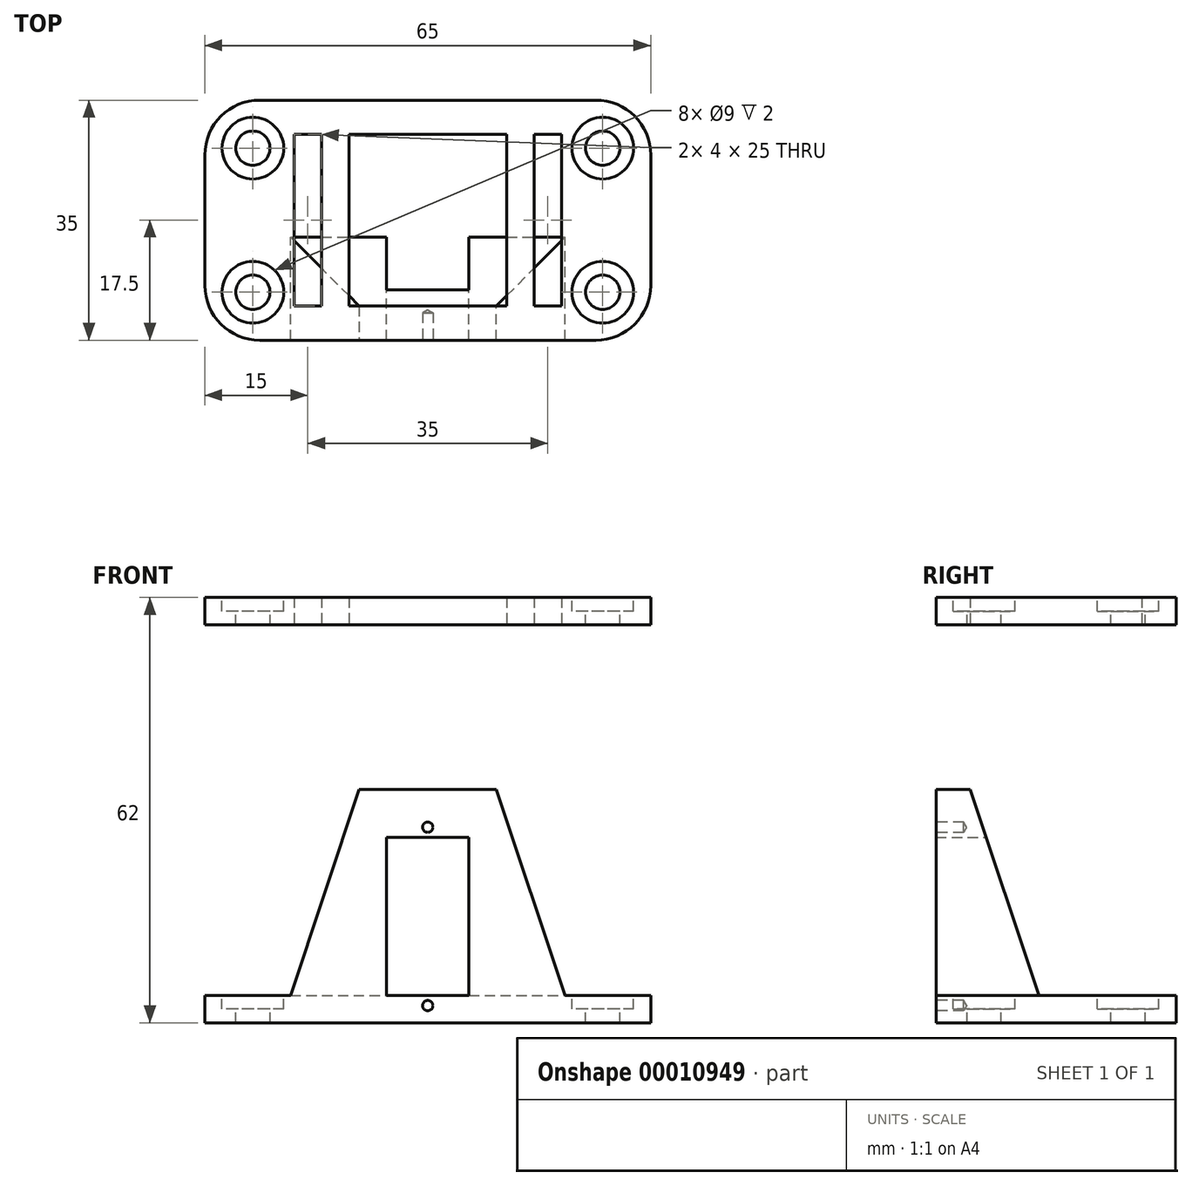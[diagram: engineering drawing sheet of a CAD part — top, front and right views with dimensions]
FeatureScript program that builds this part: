
annotation { "Feature Type Name" : "Feature", "Feature Type Description" : "" }
export const myFeature = defineFeature(function(context is Context, id is Id, definition is map)
    precondition{}
    {
        {
            var Q0;
            Q0=qCreatedBy(makeId("Top.planeOp"),FACE);
            var sketch = newSketch(context, id + "F0", { "sketchPlane" : qUnion([Q0])});
            skLineSegment(sketch, "E0.rect.bottom", {"start": v(-32.5, -17.5) * mm, "end": v(32.5, -17.5) * mm});
            skLineSegment(sketch, "E0.rect.top", {"start": v(-32.5, 17.5) * mm, "end": v(32.5, 17.5) * mm});
            skLineSegment(sketch, "E0.rect.left", {"start": v(-32.5, -17.5) * mm, "end": v(-32.5, 17.5) * mm});
            skLineSegment(sketch, "E0.rect.right", {"start": v(32.5, -17.5) * mm, "end": v(32.5, 17.5) * mm});
            skPoint(sketch, "E0.rect.middle", {"position": v(0, 0) * mm});
            skLineSegment(sketch, "E1", {"start": v(0, 0) * mm, "end": v(17.5, 0) * mm, "construction": true});
            skLineSegment(sketch, "E2.rect.bottom", {"start": v(19.5, -12.5) * mm, "end": v(15.5, -12.5) * mm});
            skLineSegment(sketch, "E2.rect.top", {"start": v(19.5, 12.5) * mm, "end": v(15.5, 12.5) * mm});
            skLineSegment(sketch, "E2.rect.left", {"start": v(19.5, -12.5) * mm, "end": v(19.5, 12.5) * mm});
            skLineSegment(sketch, "E2.rect.right", {"start": v(15.5, -12.5) * mm, "end": v(15.5, 12.5) * mm});
            skPoint(sketch, "E2.rect.middle", {"position": v(17.5, 0) * mm});
            skLineSegment(sketch, "E3", {"start": v(0, 0) * mm, "end": v(0, -46.23) * mm, "construction": true});
            skLineSegment(sketch, "E4.0.MirrorCS", {"start": v(-19.5, -12.5) * mm, "end": v(-15.5, -12.5) * mm});
            skLineSegment(sketch, "E5.0.MirrorCS", {"start": v(-19.5, -12.5) * mm, "end": v(-19.5, 12.5) * mm});
            skLineSegment(sketch, "E6.0.MirrorCS", {"start": v(-15.5, -12.5) * mm, "end": v(-15.5, 12.5) * mm});
            skLineSegment(sketch, "E7.0.MirrorCS", {"start": v(-19.5, 12.5) * mm, "end": v(-15.5, 12.5) * mm});
            skLineSegment(sketch, "E8.rect.bottom", {"start": v(11.5, -12.5) * mm, "end": v(-11.5, -12.5) * mm});
            skLineSegment(sketch, "E8.rect.top", {"start": v(11.5, 12.5) * mm, "end": v(-11.5, 12.5) * mm});
            skLineSegment(sketch, "E8.rect.left", {"start": v(11.5, -12.5) * mm, "end": v(11.5, 12.5) * mm});
            skLineSegment(sketch, "E8.rect.right", {"start": v(-11.5, -12.5) * mm, "end": v(-11.5, 12.5) * mm});
            skSolve(sketch);
        }
        {
            var Q0;
            Q0=makeQuery(id+"F0.imprint","IMPRINT",FACE,{"disambiguationData":[TD([[makeQuery(id+"F0.imprint","IMPRINT",EDGE,{"derivedFrom":sQuery(id+"F0.wireOp",EDGE,"E0.rect.bottom")}),1.0]])]});
            extrude(context, id + "F1", {"entities" : qUnion([Q0]), "depth" : 4 * mm});
        }
        {
            var Q0;
            Q0=makeQuery(id+"F1.opExtrude","CAP_FACE",FACE,{"disambiguationData":[OSD([sQuery(id+"F0.wireOp",EDGE,"E0.rect.bottom"),sQuery(id+"F0.wireOp",EDGE,"E0.rect.top"),sQuery(id+"F0.wireOp",EDGE,"E0.rect.left"),sQuery(id+"F0.wireOp",EDGE,"E0.rect.right"),sQuery(id+"F0.wireOp",EDGE,"E2.rect.bottom"),sQuery(id+"F0.wireOp",EDGE,"E2.rect.top"),sQuery(id+"F0.wireOp",EDGE,"E2.rect.left"),sQuery(id+"F0.wireOp",EDGE,"E2.rect.right"),sQuery(id+"F0.wireOp",EDGE,"E4.0.MirrorCS"),sQuery(id+"F0.wireOp",EDGE,"E5.0.MirrorCS"),sQuery(id+"F0.wireOp",EDGE,"E6.0.MirrorCS"),sQuery(id+"F0.wireOp",EDGE,"E7.0.MirrorCS")])],"isStart":false});
            var sketch = newSketch(context, id + "F2", { "sketchPlane" : qUnion([Q0])});
            skLineSegment(sketch, "E9", {"start": v(0, -17.5) * mm, "end": v(0, 17.5) * mm, "construction": true});
            skLineSegment(sketch, "E10", {"start": v(-32.5, 0) * mm, "end": v(32.5, 0) * mm, "construction": true});
            skLineSegment(sketch, "E11", {"start": v(19.5, -12.5) * mm, "end": v(25.5, -12.5) * mm, "construction": true});
            skLineSegment(sketch, "E12", {"start": v(25.5, -12.5) * mm, "end": v(25.5, -10.5) * mm, "construction": true});
            skPoint(sketch, "E13", {"position": v(25.5, -10.5) * mm});
            skPoint(sketch, "E14.0.MirrorP", {"position": v(-25.5, -10.5) * mm});
            skPoint(sketch, "E15.0.MirrorP", {"position": v(-25.5, 10.5) * mm});
            skPoint(sketch, "E16.0.MirrorP", {"position": v(25.5, 10.5) * mm});
            skSolve(sketch);
        }
        {
            var Q0;
            Q0=sQuery(id+"F2.wireOp",VERTEX,"E15.0.MirrorP");
            var Q1;
            Q1=sQuery(id+"F2.wireOp",VERTEX,"E16.0.MirrorP");
            var Q2;
            Q2=sQuery(id+"F2.wireOp",VERTEX,"E13");
            var Q3;
            Q3=sQuery(id+"F2.wireOp",VERTEX,"E14.0.MirrorP");
            var Q4;
            Q4=makeQuery(id+"F1.opExtrude","SWEPT_BODY",BODY,{"disambiguationData":[OSD([sQuery(id+"F0.wireOp",EDGE,"E0.rect.bottom"),sQuery(id+"F0.wireOp",EDGE,"E0.rect.top"),sQuery(id+"F0.wireOp",EDGE,"E0.rect.left"),sQuery(id+"F0.wireOp",EDGE,"E0.rect.right"),sQuery(id+"F0.wireOp",EDGE,"E2.rect.bottom"),sQuery(id+"F0.wireOp",EDGE,"E2.rect.top"),sQuery(id+"F0.wireOp",EDGE,"E2.rect.left"),sQuery(id+"F0.wireOp",EDGE,"E2.rect.right"),sQuery(id+"F0.wireOp",EDGE,"E4.0.MirrorCS"),sQuery(id+"F0.wireOp",EDGE,"E5.0.MirrorCS"),sQuery(id+"F0.wireOp",EDGE,"E6.0.MirrorCS"),sQuery(id+"F0.wireOp",EDGE,"E7.0.MirrorCS")])]});
            hole(context, id + "F3", {"style" : HoleStyle.C_BORE, "holeDiameter" : 5 * mm, "cBoreDiameter" : 9 * mm, "cBoreDepth" : 2 * mm, "endStyle" : HoleEndStyle.THROUGH, "locations" : qUnion([Q0, Q1, Q2, Q3]), "scope" : qUnion([Q4])});
        }
        {
            var Q0;
            Q0=makeQuery(id+"F1.opExtrude","SWEPT_EDGE",EDGE,{"disambiguationData":[OSD([sQuery(id+"F0.wireOp",EDGE,"E0.rect.bottom"),sQuery(id+"F0.wireOp",EDGE,"E0.rect.left")])]});
            var Q1;
            Q1=makeQuery(id+"F1.opExtrude","SWEPT_EDGE",EDGE,{"disambiguationData":[OSD([sQuery(id+"F0.wireOp",EDGE,"E0.rect.bottom"),sQuery(id+"F0.wireOp",EDGE,"E0.rect.right")])]});
            var Q2;
            Q2=makeQuery(id+"F1.opExtrude","SWEPT_EDGE",EDGE,{"disambiguationData":[OSD([sQuery(id+"F0.wireOp",EDGE,"E0.rect.top"),sQuery(id+"F0.wireOp",EDGE,"E0.rect.right")])]});
            var Q3;
            Q3=makeQuery(id+"F1.opExtrude","SWEPT_EDGE",EDGE,{"disambiguationData":[OSD([sQuery(id+"F0.wireOp",EDGE,"E0.rect.top"),sQuery(id+"F0.wireOp",EDGE,"E0.rect.left")])]});
            fillet(context, id + "F4", {"entities" : qUnion([Q0, Q1, Q2, Q3]), "radius" : 8 * mm, "tangentPropagation" : true, "allowEdgeOverflow" : false});
        }
        {
            var Q0;
            Q0 = qSketchRegion(id + "F0", true);
            var Q1;
            Q1=makeQuery(id+"F0.imprint","IMPRINT",FACE,{"disambiguationData":[TD([[makeQuery(id+"F0.imprint","IMPRINT",EDGE,{"derivedFrom":sQuery(id+"F0.wireOp",EDGE,"E8.rect.bottom")}),-1.0]])]});
            var Q2;
            Q2=makeQuery(id+"F0.imprint","IMPRINT",FACE,{"disambiguationData":[TD([[makeQuery(id+"F0.imprint","IMPRINT",EDGE,{"derivedFrom":sQuery(id+"F0.wireOp",EDGE,"E4.0.MirrorCS")}),1.0]])]});
            var Q3;
            Q3=makeQuery(id+"F0.imprint","IMPRINT",FACE,{"disambiguationData":[TD([[makeQuery(id+"F0.imprint","IMPRINT",EDGE,{"derivedFrom":sQuery(id+"F0.wireOp",EDGE,"E2.rect.bottom")}),-1.0]])]});
            extrude(context, id + "F5", {"entities" : qUnion([Q0, Q1, Q2, Q3]), "oppositeDirection" : true, "depth" : 8 * mm});
        }
        {
            var Q0;
            Q0 = qSketchRegion(id + "F0", true);
            var Q1;
            Q1=makeQuery(id+"F0.imprint","IMPRINT",FACE,{"disambiguationData":[TD([[makeQuery(id+"F0.imprint","IMPRINT",EDGE,{"derivedFrom":sQuery(id+"F0.wireOp",EDGE,"E2.rect.bottom")}),-1.0]])]});
            var Q2;
            Q2=makeQuery(id+"F0.imprint","IMPRINT",FACE,{"disambiguationData":[TD([[makeQuery(id+"F0.imprint","IMPRINT",EDGE,{"derivedFrom":sQuery(id+"F0.wireOp",EDGE,"E8.rect.bottom")}),-1.0]])]});
            var Q3;
            Q3=makeQuery(id+"F0.imprint","IMPRINT",FACE,{"disambiguationData":[TD([[makeQuery(id+"F0.imprint","IMPRINT",EDGE,{"derivedFrom":sQuery(id+"F0.wireOp",EDGE,"E4.0.MirrorCS")}),1.0]])]});
            extrude(context, id + "F6", {"entities" : qUnion([Q0, Q1, Q2, Q3]), "operationType" : NewBodyOperationType.REMOVE, "oppositeDirection" : true, "depth" : 4 * mm});
        }
        {
            var Q0;
            Q0=makeQuery(id+"F6.boolean.opBoolean","COPY",FACE,{"derivedFrom":makeQuery(id+"F6.opExtrude","CAP_FACE",FACE,{"disambiguationData":[OSD([sQuery(id+"F0.wireOp",EDGE,"E0.rect.bottom"),sQuery(id+"F0.wireOp",EDGE,"E0.rect.top"),sQuery(id+"F0.wireOp",EDGE,"E0.rect.left"),sQuery(id+"F0.wireOp",EDGE,"E0.rect.right")])],"isStart":false})});
            var sketch = newSketch(context, id + "F7", { "sketchPlane" : qUnion([Q0])});
            skLineSegment(sketch, "E17", {"start": v(0, 0) * mm, "end": v(32.5, 0) * mm, "construction": true});
            skLineSegment(sketch, "E18", {"start": v(0, 0) * mm, "end": v(0, -17.5) * mm, "construction": true});
            skLineSegment(sketch, "E19", {"start": v(25.5, 0) * mm, "end": v(25.5, -10.5) * mm, "construction": true});
            skPoint(sketch, "E20", {"position": v(25.5, -10.5) * mm});
            skPoint(sketch, "E21.0.MirrorP", {"position": v(25.5, 10.5) * mm});
            skLineSegment(sketch, "E22.0.MirrorCS", {"start": v(0, 0) * mm, "end": v(0, 17.5) * mm, "construction": true});
            skPoint(sketch, "E23.0.MirrorP", {"position": v(-25.5, 10.5) * mm});
            skPoint(sketch, "E24.0.MirrorP", {"position": v(-25.5, -10.5) * mm});
            skSolve(sketch);
        }
        {
            var Q0;
            Q0=sQuery(id+"F7.wireOp",VERTEX,"E20");
            var Q1;
            Q1=sQuery(id+"F7.wireOp",VERTEX,"E21.0.MirrorP");
            var Q2;
            Q2=sQuery(id+"F7.wireOp",VERTEX,"E24.0.MirrorP");
            var Q3;
            Q3=sQuery(id+"F7.wireOp",VERTEX,"E23.0.MirrorP");
            var Q4;
            Q4=makeQuery(id+"F5.opExtrude","SWEPT_BODY",BODY,{"disambiguationData":[OSD([sQuery(id+"F0.wireOp",EDGE,"E0.rect.bottom"),sQuery(id+"F0.wireOp",EDGE,"E0.rect.top"),sQuery(id+"F0.wireOp",EDGE,"E0.rect.left"),sQuery(id+"F0.wireOp",EDGE,"E0.rect.right")])]});
            hole(context, id + "F8", {"style" : HoleStyle.C_BORE, "holeDiameter" : 5 * mm, "cBoreDiameter" : 9 * mm, "cBoreDepth" : 2 * mm, "endStyle" : HoleEndStyle.THROUGH, "locations" : qUnion([Q0, Q1, Q2, Q3]), "scope" : qUnion([Q4])});
        }
        {
            var Q0;
            Q0=makeQuery(id+"F5.opExtrude","SWEPT_EDGE",EDGE,{"disambiguationData":[OSD([sQuery(id+"F0.wireOp",EDGE,"E0.rect.top"),sQuery(id+"F0.wireOp",EDGE,"E0.rect.left")])]});
            var Q1;
            Q1=makeQuery(id+"F5.opExtrude","SWEPT_EDGE",EDGE,{"disambiguationData":[OSD([sQuery(id+"F0.wireOp",EDGE,"E0.rect.bottom"),sQuery(id+"F0.wireOp",EDGE,"E0.rect.left")])]});
            var Q2;
            Q2=makeQuery(id+"F5.opExtrude","SWEPT_EDGE",EDGE,{"disambiguationData":[OSD([sQuery(id+"F0.wireOp",EDGE,"E0.rect.top"),sQuery(id+"F0.wireOp",EDGE,"E0.rect.right")])]});
            var Q3;
            Q3=makeQuery(id+"F5.opExtrude","SWEPT_EDGE",EDGE,{"disambiguationData":[OSD([sQuery(id+"F0.wireOp",EDGE,"E0.rect.bottom"),sQuery(id+"F0.wireOp",EDGE,"E0.rect.right")])]});
            fillet(context, id + "F9", {"entities" : qUnion([Q0, Q1, Q2, Q3]), "radius" : 8 * mm, "tangentPropagation" : true, "allowEdgeOverflow" : false});
        }
        {
            var Q0;
            Q0=makeQuery(id+"F5.opExtrude","SWEPT_BODY",BODY,{"disambiguationData":[OSD([sQuery(id+"F0.wireOp",EDGE,"E0.rect.bottom"),sQuery(id+"F0.wireOp",EDGE,"E0.rect.top"),sQuery(id+"F0.wireOp",EDGE,"E0.rect.left"),sQuery(id+"F0.wireOp",EDGE,"E0.rect.right")])]});
            transform(context, id + "F10", {"entities" : qUnion([Q0]), "transformType" : TransformType.TRANSLATION_3D, "dx" : 0 * mm, "dy" : 0 * mm, "dz" : -50 * mm, "makeCopy" : false});
        }
        {
            var Q0;
            Q0=makeQuery(id+"F6.boolean.opBoolean","COPY",FACE,{"derivedFrom":makeQuery(id+"F6.opExtrude","CAP_FACE",FACE,{"disambiguationData":[OSD([sQuery(id+"F0.wireOp",EDGE,"E0.rect.bottom"),sQuery(id+"F0.wireOp",EDGE,"E0.rect.top"),sQuery(id+"F0.wireOp",EDGE,"E0.rect.left"),sQuery(id+"F0.wireOp",EDGE,"E0.rect.right")])],"isStart":false})});
            var sketch = newSketch(context, id + "F11", { "sketchPlane" : qUnion([Q0])});
            skLineSegment(sketch, "E25.bottom", {"start": v(0, -17.5) * mm, "end": v(20, -17.5) * mm});
            skLineSegment(sketch, "E25.top", {"start": v(0, -2.5) * mm, "end": v(20, -2.5) * mm});
            skLineSegment(sketch, "E25.left", {"start": v(0, -17.5) * mm, "end": v(0, -2.5) * mm, "construction": true});
            skLineSegment(sketch, "E25.right", {"start": v(20, -17.5) * mm, "end": v(20, -2.5) * mm});
            skLineSegment(sketch, "E26.0.MirrorCS", {"start": v(0, -2.5) * mm, "end": v(-20, -2.5) * mm});
            skLineSegment(sketch, "E27.0.MirrorCS", {"start": v(-20, -17.5) * mm, "end": v(-20, -2.5) * mm});
            skSolve(sketch);
        }
        {
            var Q0;
            {var subQ2=sQuery(id+"F11.wireOp",EDGE,"E25.bottom");Q0=makeQuery(id+"F11.imprint","IMPRINT",FACE,{"disambiguationData":[TD([[makeQuery(id+"F11.imprint","IMPRINT",EDGE,{"derivedFrom":subQ2}),1.0]])]});}
            extrude(context, id + "F12", {"entities" : qUnion([Q0]), "operationType" : NewBodyOperationType.ADD, "depth" : 30 * mm});
        }
        {
            var Q0;
            Q0=makeQuery(id+"F12.opExtrude","SWEPT_FACE",FACE,{"disambiguationData":[OSD([sQuery(id+"F11.wireOp",EDGE,"E25.top"),sQuery(id+"F11.wireOp",EDGE,"E26.0.MirrorCS")])]});
            var sketch = newSketch(context, id + "F13", { "sketchPlane" : qUnion([Q0])});
            skLineSegment(sketch, "E28.bottom", {"start": v(0, -54) * mm, "end": v(6, -54) * mm});
            skLineSegment(sketch, "E28.top", {"start": v(0, -31) * mm, "end": v(6, -31) * mm});
            skLineSegment(sketch, "E28.left", {"start": v(0, -54) * mm, "end": v(0, -31) * mm, "construction": true});
            skLineSegment(sketch, "E28.right", {"start": v(6, -54) * mm, "end": v(6, -31) * mm});
            skLineSegment(sketch, "E29.0.MirrorCS", {"start": v(0, -31) * mm, "end": v(-6, -31) * mm});
            skLineSegment(sketch, "E30.0.MirrorCS", {"start": v(-6, -54) * mm, "end": v(-6, -31) * mm});
            skSolve(sketch);
        }
        {
            var Q0;
            {var subQ2=sQuery(id+"F13.wireOp",EDGE,"E28.bottom");Q0=makeQuery(id+"F13.imprint","IMPRINT",FACE,{"disambiguationData":[TD([[makeQuery(id+"F13.imprint","IMPRINT",EDGE,{"derivedFrom":subQ2}),-1.0]])]});}
            extrude(context, id + "F14", {"entities" : qUnion([Q0]), "operationType" : NewBodyOperationType.REMOVE, "endBound" : BoundingType.UP_TO_NEXT, "oppositeDirection" : true, "depth" : 25 * mm});
        }
        {
            var Q0;
            Q0=makeQuery(id+"F12.opExtrude","CAP_EDGE",EDGE,{"disambiguationData":[OSD([sQuery(id+"F11.wireOp",EDGE,"E27.0.MirrorCS")])],"isStart":false});
            var Q1;
            Q1=makeQuery(id+"F12.opExtrude","CAP_EDGE",EDGE,{"disambiguationData":[OSD([sQuery(id+"F11.wireOp",EDGE,"E25.right")])],"isStart":false});
            var Q2;
            Q2=makeQuery(id+"F12.opExtrude","CAP_EDGE",EDGE,{"disambiguationData":[OSD([sQuery(id+"F11.wireOp",EDGE,"E25.top"),sQuery(id+"F11.wireOp",EDGE,"E26.0.MirrorCS")])],"isStart":false});
            chamfer(context, id + "F15", {"entities" : qUnion([Q0, Q1, Q2]), "chamferType" : ChamferType.TWO_OFFSETS, "width1" : 30 * mm, "oppositeDirection" : false, "width2" : 10 * mm, "tangentPropagation" : true});
        }
        {
            var Q0;
            {var subQ0=sQuery(id+"F0.wireOp",EDGE,"E0.rect.bottom");Q0=makeQuery(id+"F12.boolean.opBoolean","MERGE",FACE,{"derivedFrom":[makeQuery(id+"F5.opExtrude","SWEPT_FACE",FACE,{"disambiguationData":[OSD([subQ0])]}),makeQuery(id+"F12.opExtrude","SWEPT_FACE",FACE,{"disambiguationData":[OSD([subQ0,sQuery(id+"F11.wireOp",EDGE,"E25.bottom")])]})]});}
            var sketch = newSketch(context, id + "F16", { "sketchPlane" : qUnion([Q0])});
            skLineSegment(sketch, "E31", {"start": v(0, -54) * mm, "end": v(0, -55.5) * mm, "construction": true});
            skLineSegment(sketch, "E32", {"start": v(-6, -42.5) * mm, "end": v(6, -42.5) * mm, "construction": true});
            skPoint(sketch, "E33", {"position": v(0, -55.5) * mm});
            skPoint(sketch, "E34.0.MirrorP", {"position": v(0, -29.5) * mm});
            skSolve(sketch);
        }
        {
            var Q0;
            Q0=sQuery(id+"F16.wireOp",VERTEX,"E34.0.MirrorP");
            var Q1;
            Q1=sQuery(id+"F16.wireOp",VERTEX,"E33");
            var Q2;
            Q2=makeQuery(id+"F5.opExtrude","SWEPT_BODY",BODY,{"disambiguationData":[OSD([sQuery(id+"F0.wireOp",EDGE,"E0.rect.bottom"),sQuery(id+"F0.wireOp",EDGE,"E0.rect.top"),sQuery(id+"F0.wireOp",EDGE,"E0.rect.left"),sQuery(id+"F0.wireOp",EDGE,"E0.rect.right")])]});
            hole(context, id + "F17", {"style" : HoleStyle.SIMPLE, "holeDiameter" : 1.5 * mm, "endStyle" : HoleEndStyle.BLIND, "holeDepth" : 4 * mm, "locations" : qUnion([Q0, Q1]), "scope" : qUnion([Q2])});
        }
    });
